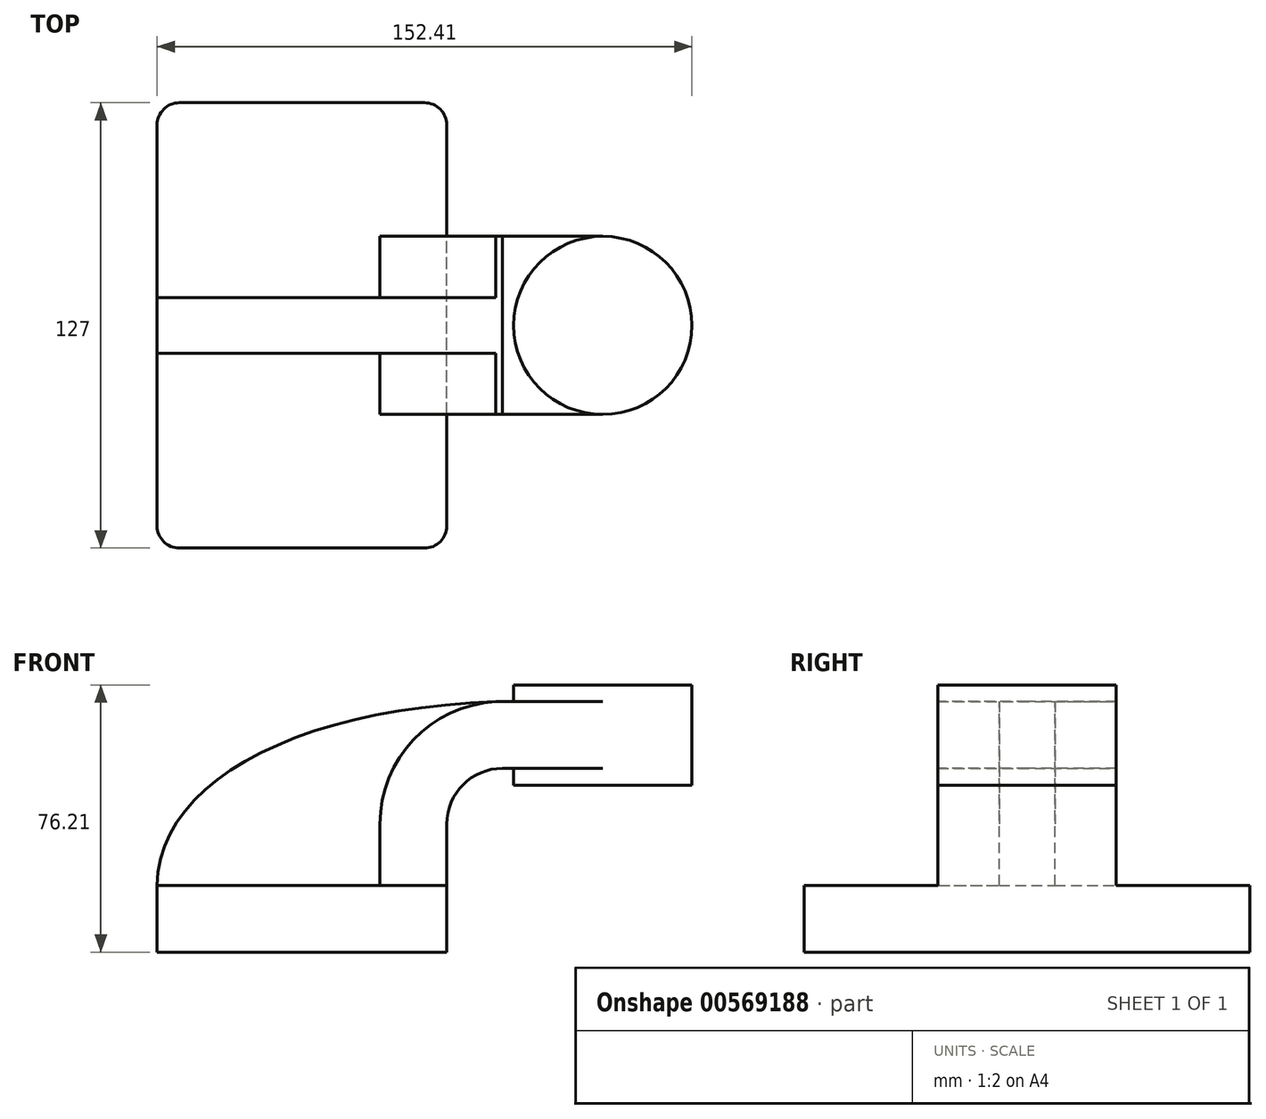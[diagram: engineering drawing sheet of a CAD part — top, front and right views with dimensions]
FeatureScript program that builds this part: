
annotation { "Feature Type Name" : "Feature", "Feature Type Description" : "" }
export const myFeature = defineFeature(function(context is Context, id is Id, definition is map)
    precondition{}
    {
        {
            var Q0;
            Q0=qCreatedBy(makeId("Front.planeOp"),FACE);
            var sketch = newSketch(context, id + "F0", { "sketchPlane" : qUnion([Q0])});
            skLineSegment(sketch, "E0.bottom", {"start": v(-41.28, -9.53) * mm, "end": v(41.28, -9.53) * mm});
            skLineSegment(sketch, "E0.top", {"start": v(-41.28, 9.53) * mm, "end": v(41.28, 9.53) * mm});
            skLineSegment(sketch, "E0.left", {"start": v(-41.28, -9.53) * mm, "end": v(-41.28, 9.53) * mm});
            skLineSegment(sketch, "E0.right", {"start": v(41.28, -9.53) * mm, "end": v(41.28, 9.53) * mm});
            skPoint(sketch, "E0.middle", {"position": v(0, 0) * mm});
            skLineSegment(sketch, "E1.bottom", {"start": v(60.33, 38.1) * mm, "end": v(111.13, 38.1) * mm});
            skLineSegment(sketch, "E1.top", {"start": v(60.33, 66.68) * mm, "end": v(111.13, 66.68) * mm});
            skLineSegment(sketch, "E1.left", {"start": v(60.33, 38.1) * mm, "end": v(60.32, 66.67) * mm});
            skLineSegment(sketch, "E1.right", {"start": v(111.13, 38.1) * mm, "end": v(111.13, 66.68) * mm});
            skPoint(sketch, "E1.middle", {"position": v(85.73, 52.39) * mm});
            skLineSegment(sketch, "E2", {"start": v(41.28, 9.53) * mm, "end": v(41.28, 27) * mm});
            skArc(sketch, "E3", {"start": v(41.27, 27) * mm, "mid": v(45.92, 38.23) * mm, "end": v(57.15, 42.88) * mm});
            skLineSegment(sketch, "E4", {"start": v(57.15, 42.88) * mm, "end": v(85.73, 42.88) * mm});
            skLineSegment(sketch, "E5.0", {"start": v(57.15, 61.93) * mm, "end": v(85.73, 61.93) * mm});
            skArc(sketch, "E5.1", {"start": v(22.22, 27) * mm, "mid": v(32.45, 51.7) * mm, "end": v(57.15, 61.93) * mm});
            skLineSegment(sketch, "E5.2", {"start": v(22.22, 9.53) * mm, "end": v(22.22, 27) * mm});
            skPoint(sketch, "E6.startSnap0", {"position": v(45.92, 38.23) * mm});
            skFitSpline(sketch, "E7", {"points": [v(-41.28, 9.53) * mm, v(57.15, 61.93) * mm], "startDerivative": vector(0.9, 89.83) * mm, "endDerivative": vector(171.45, 4.15) * mm});
            skLineSegment(sketch, "E8", {"start": v(85.73, 38.1) * mm, "end": v(85.73, 66.68) * mm});
            skSolve(sketch);
        }
        {
            var Q0;
            Q0=makeQuery(id+"F0.imprint","IMPRINT",FACE,{"disambiguationData":[TD([[makeQuery(id+"F0.imprint","IMPRINT",EDGE,{"derivedFrom":sQuery(id+"F0.wireOp",EDGE,"E0.bottom")}),1.0]])]});
            extrude(context, id + "F1", {"entities" : qUnion([Q0]), "endBound" : BoundingType.SYMMETRIC, "depth" : 127 * mm, "offsetDistance" : 25.4 * mm});
        }
        {
            var Q0;
            {var subQ1=sQuery(id+"F0.wireOp",EDGE,"E2");Q0=makeQuery(id+"F0.imprint","IMPRINT",FACE,{"disambiguationData":[TD([[makeQuery(id+"F0.imprint","IMPRINT",EDGE,{"derivedFrom":subQ1}),1.0]])]});}
            var Q1;
            {var subQ0=sQuery(id+"F0.wireOp",EDGE,"E4");var subQ1=sQuery(id+"F0.wireOp",EDGE,"E1.left");var subQ2=makeQuery(id+"F0.imprint","INTERSECT",VERTEX,{"derivedFrom":[subQ1,subQ0]});Q1=makeQuery(id+"F0.imprint","IMPRINT",FACE,{"disambiguationData":[TD([[makeQuery(id+"F0.imprint","IMPRINT",EDGE,{"disambiguationData":[TD([[subQ2,-1.0]])],"derivedFrom":subQ1}),-1.0]])]});}
            extrude(context, id + "F2", {"entities" : qUnion([Q0, Q1]), "operationType" : NewBodyOperationType.ADD, "endBound" : BoundingType.SYMMETRIC, "depth" : 50.8 * mm, "offsetDistance" : 25.4 * mm});
        }
        {
            var Q0;
            {var subQ3=sQuery(id+"F0.wireOp",EDGE,"E5.2");Q0=makeQuery(id+"F0.imprint","IMPRINT",FACE,{"disambiguationData":[TD([[makeQuery(id+"F0.imprint","IMPRINT",EDGE,{"derivedFrom":subQ3}),1.0]])]});}
            extrude(context, id + "F3", {"entities" : qUnion([Q0]), "operationType" : NewBodyOperationType.ADD, "endBound" : BoundingType.SYMMETRIC, "depth" : 15.88 * mm, "offsetDistance" : 25.4 * mm});
        }
        {
            var Q0;
            {var subQ4=sQuery(id+"F0.wireOp",EDGE,"E1.right");Q0=makeQuery(id+"F0.imprint","IMPRINT",FACE,{"disambiguationData":[TD([[makeQuery(id+"F0.imprint","IMPRINT",EDGE,{"derivedFrom":subQ4}),1.0]])]});}
            var Q1;
            Q1=sQuery(id+"F0.wireOp",EDGE,"E8");
            revolve(context, id + "F4", {"operationType" : NewBodyOperationType.ADD, "entities" : qUnion([Q0]), "axis" : qUnion([Q1]), "revolveType" : RevolveType.FULL});
        }
        {
            var Q0;
            Q0=makeQuery(id+"F1.opExtrude","CAP_EDGE",EDGE,{"disambiguationData":[OSD([sQuery(id+"F0.wireOp",EDGE,"E0.right")])],"isStart":false});
            var Q1;
            Q1=makeQuery(id+"F1.opExtrude","CAP_EDGE",EDGE,{"disambiguationData":[OSD([sQuery(id+"F0.wireOp",EDGE,"E0.left")])],"isStart":false});
            var Q2;
            Q2=makeQuery(id+"F1.opExtrude","CAP_EDGE",EDGE,{"disambiguationData":[OSD([sQuery(id+"F0.wireOp",EDGE,"E0.right")])],"isStart":true});
            var Q3;
            Q3=makeQuery(id+"F1.opExtrude","CAP_EDGE",EDGE,{"disambiguationData":[OSD([sQuery(id+"F0.wireOp",EDGE,"E0.left")])],"isStart":true});
            fillet(context, id + "F5", {"entities" : qUnion([Q0, Q1, Q2, Q3]), "radius" : 6.35 * mm, "tangentPropagation" : true, "allowEdgeOverflow" : false});
        }
    });
